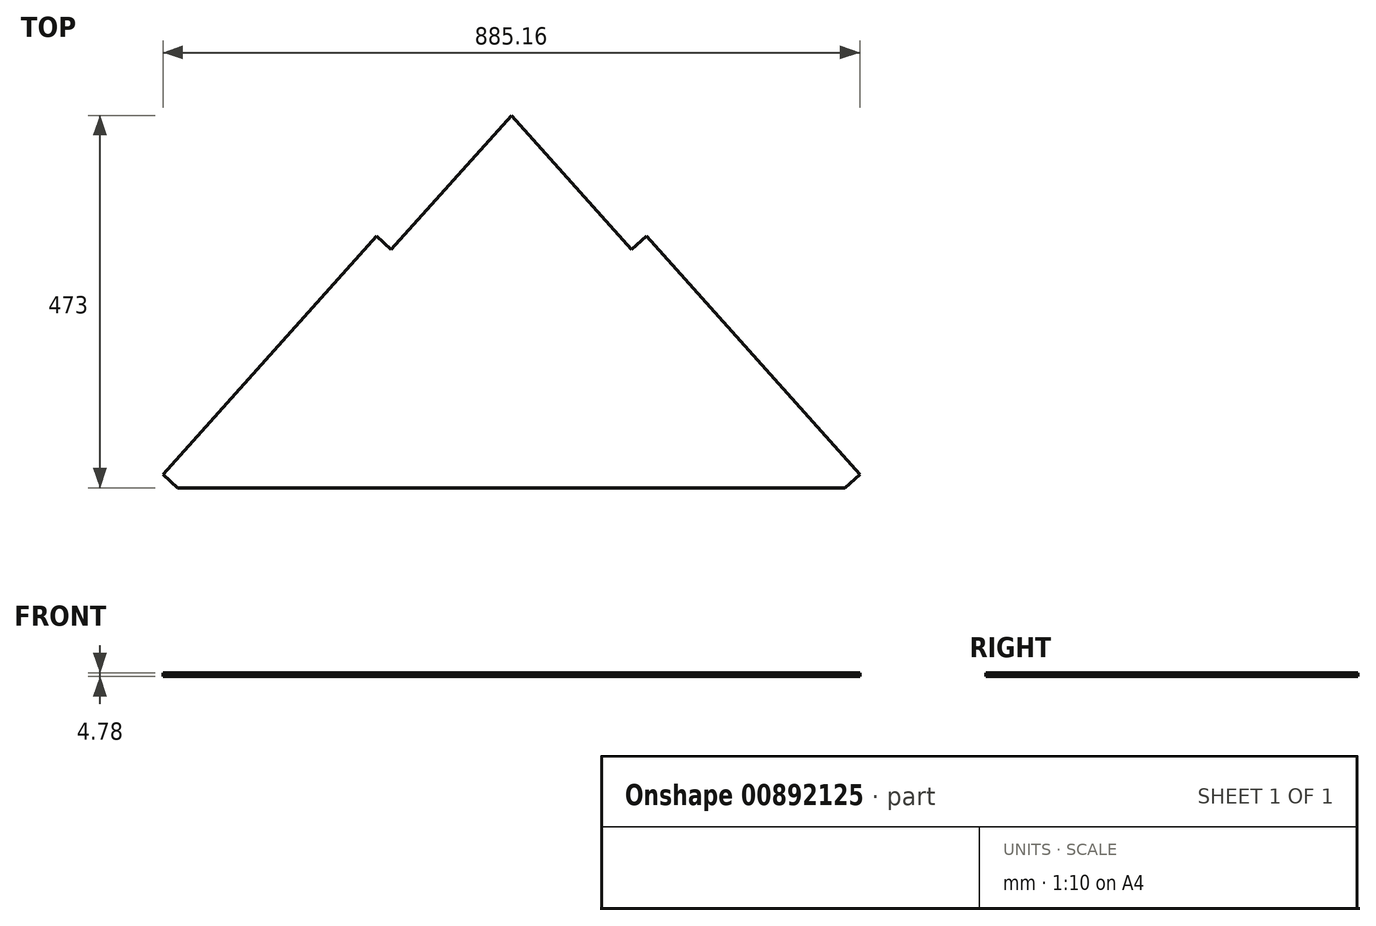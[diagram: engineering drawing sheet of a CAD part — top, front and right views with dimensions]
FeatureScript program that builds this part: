
annotation { "Feature Type Name" : "Feature", "Feature Type Description" : "" }
export const myFeature = defineFeature(function(context is Context, id is Id, definition is map)
    precondition{}
    {
        {
            var Q0;
            Q0=qCreatedBy(makeId("Top.planeOp"),FACE);
            var sketch = newSketch(context, id + "F0", { "sketchPlane" : qUnion([Q0])});
            skLineSegment(sketch, "E0", {"start": v(0, 222.35) * mm, "end": v(-423.66, -250.65) * mm});
            skLineSegment(sketch, "E1", {"start": v(0, 222.35) * mm, "end": v(423.66, -250.65) * mm});
            skLineSegment(sketch, "E2", {"start": v(-423.66, -250.65) * mm, "end": v(423.66, -250.65) * mm});
            skSolve(sketch);
        }
        {
            var Q0;
            Q0 = qSketchRegion(id + "F0", true);
            extrude(context, id + "F1", {"entities" : qUnion([Q0]), "depth" : 4.78 * mm, "offsetDistance" : 25.4 * mm});
        }
        {
            var Q0;
            Q0=makeQuery(id+"F1.opExtrude","SWEPT_FACE",FACE,{"disambiguationData":[OSD([sQuery(id+"F0.wireOp",EDGE,"E1")])]});
            var sketch = newSketch(context, id + "F2", { "sketchPlane" : qUnion([Q0])});
            skLineSegment(sketch, "E3.bottom", {"start": v(-469.37, 4.78) * mm, "end": v(-62.97, 4.78) * mm});
            skLineSegment(sketch, "E3.top", {"start": v(-469.37, 0) * mm, "end": v(-62.97, 0) * mm});
            skLineSegment(sketch, "E3.left", {"start": v(-469.37, 4.78) * mm, "end": v(-469.37, 0) * mm});
            skLineSegment(sketch, "E3.right", {"start": v(-62.97, 4.78) * mm, "end": v(-62.97, 0) * mm});
            skSolve(sketch);
        }
        {
            var Q0;
            Q0 = qSketchRegion(id + "F2", true);
            extrude(context, id + "F3", {"entities" : qUnion([Q0]), "operationType" : NewBodyOperationType.ADD, "depth" : 25.4 * mm, "offsetDistance" : 25.4 * mm});
        }
        {
            var Q0;
            Q0=makeQuery(id+"F1.opExtrude","SWEPT_FACE",FACE,{"disambiguationData":[OSD([sQuery(id+"F0.wireOp",EDGE,"E0")])]});
            var sketch = newSketch(context, id + "F4", { "sketchPlane" : qUnion([Q0])});
            skLineSegment(sketch, "E4.bottom", {"start": v(469.37, 4.78) * mm, "end": v(62.97, 4.78) * mm});
            skLineSegment(sketch, "E4.top", {"start": v(469.37, 0) * mm, "end": v(62.97, 0) * mm});
            skLineSegment(sketch, "E4.left", {"start": v(469.37, 4.78) * mm, "end": v(469.37, 0) * mm});
            skLineSegment(sketch, "E4.right", {"start": v(62.97, 4.78) * mm, "end": v(62.97, 0) * mm});
            skSolve(sketch);
        }
        {
            var Q0;
            Q0 = qSketchRegion(id + "F4", true);
            extrude(context, id + "F5", {"entities" : qUnion([Q0]), "operationType" : NewBodyOperationType.ADD, "depth" : 25.4 * mm, "offsetDistance" : 25.4 * mm});
        }
    });
